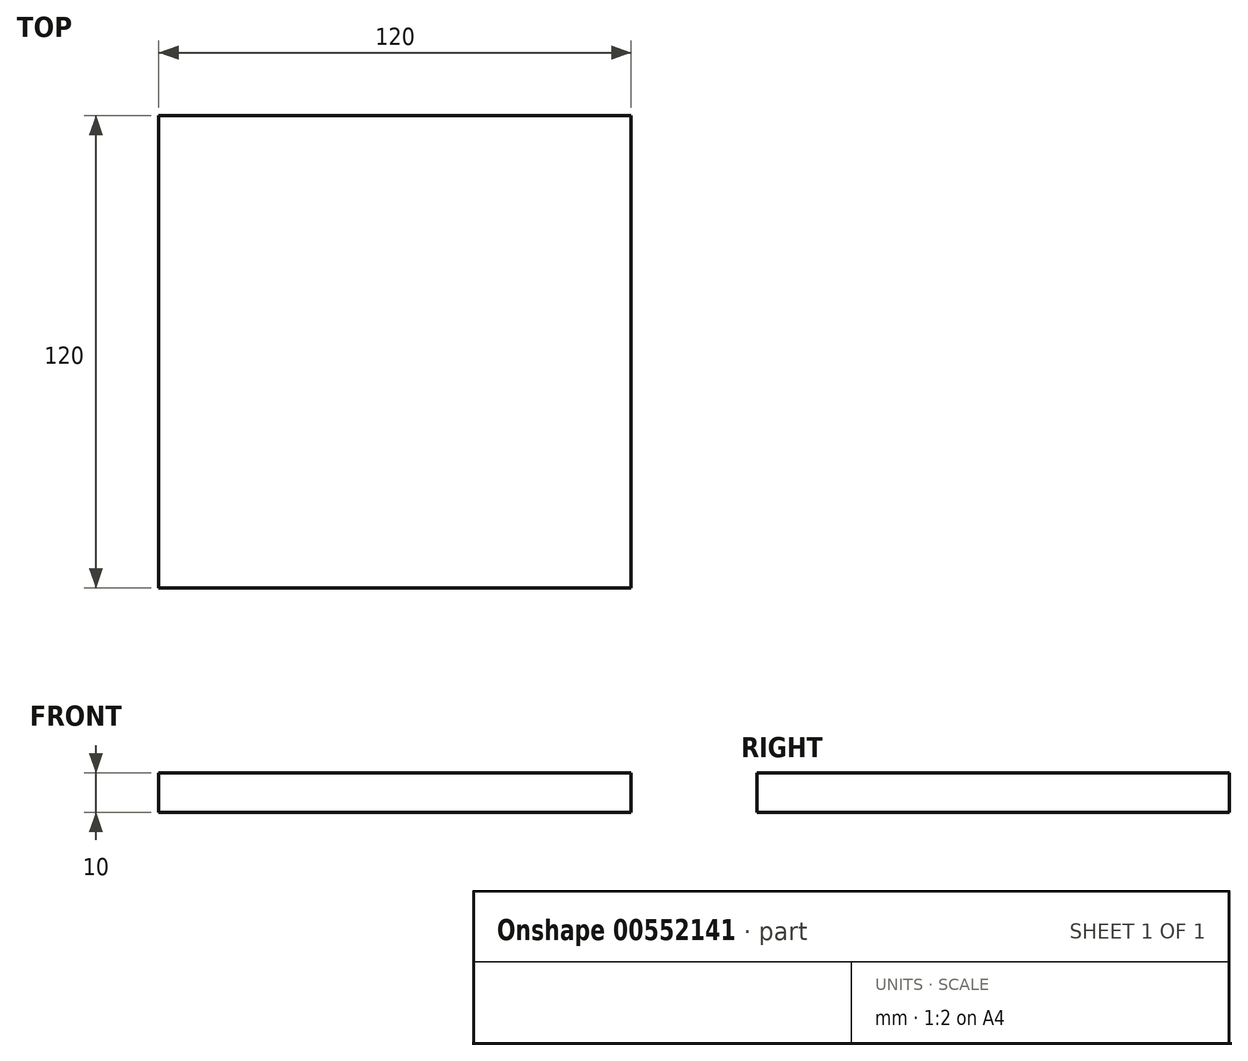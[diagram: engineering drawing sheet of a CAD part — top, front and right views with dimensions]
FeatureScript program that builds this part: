
annotation { "Feature Type Name" : "Feature", "Feature Type Description" : "" }
export const myFeature = defineFeature(function(context is Context, id is Id, definition is map)
    precondition{}
    {
        {
            var Q0;
            Q0=qCreatedBy(makeId("Top.planeOp"),FACE);
            var sketch = newSketch(context, id + "F0", { "sketchPlane" : qUnion([Q0])});
            skLineSegment(sketch, "E0.bottom", {"start": v(-60, -60) * mm, "end": v(60, -60) * mm});
            skLineSegment(sketch, "E0.top", {"start": v(-60, 60) * mm, "end": v(60, 60) * mm});
            skLineSegment(sketch, "E0.left", {"start": v(-60, -60) * mm, "end": v(-60, 60) * mm});
            skLineSegment(sketch, "E0.right", {"start": v(60, -60) * mm, "end": v(60, 60) * mm});
            skSolve(sketch);
        }
        {
            var Q0;
            Q0 = qSketchRegion(id + "F0", true);
            extrude(context, id + "F1", {"entities" : qUnion([Q0]), "depth" : 10 * mm, "offsetDistance" : 25 * mm});
        }
    });
